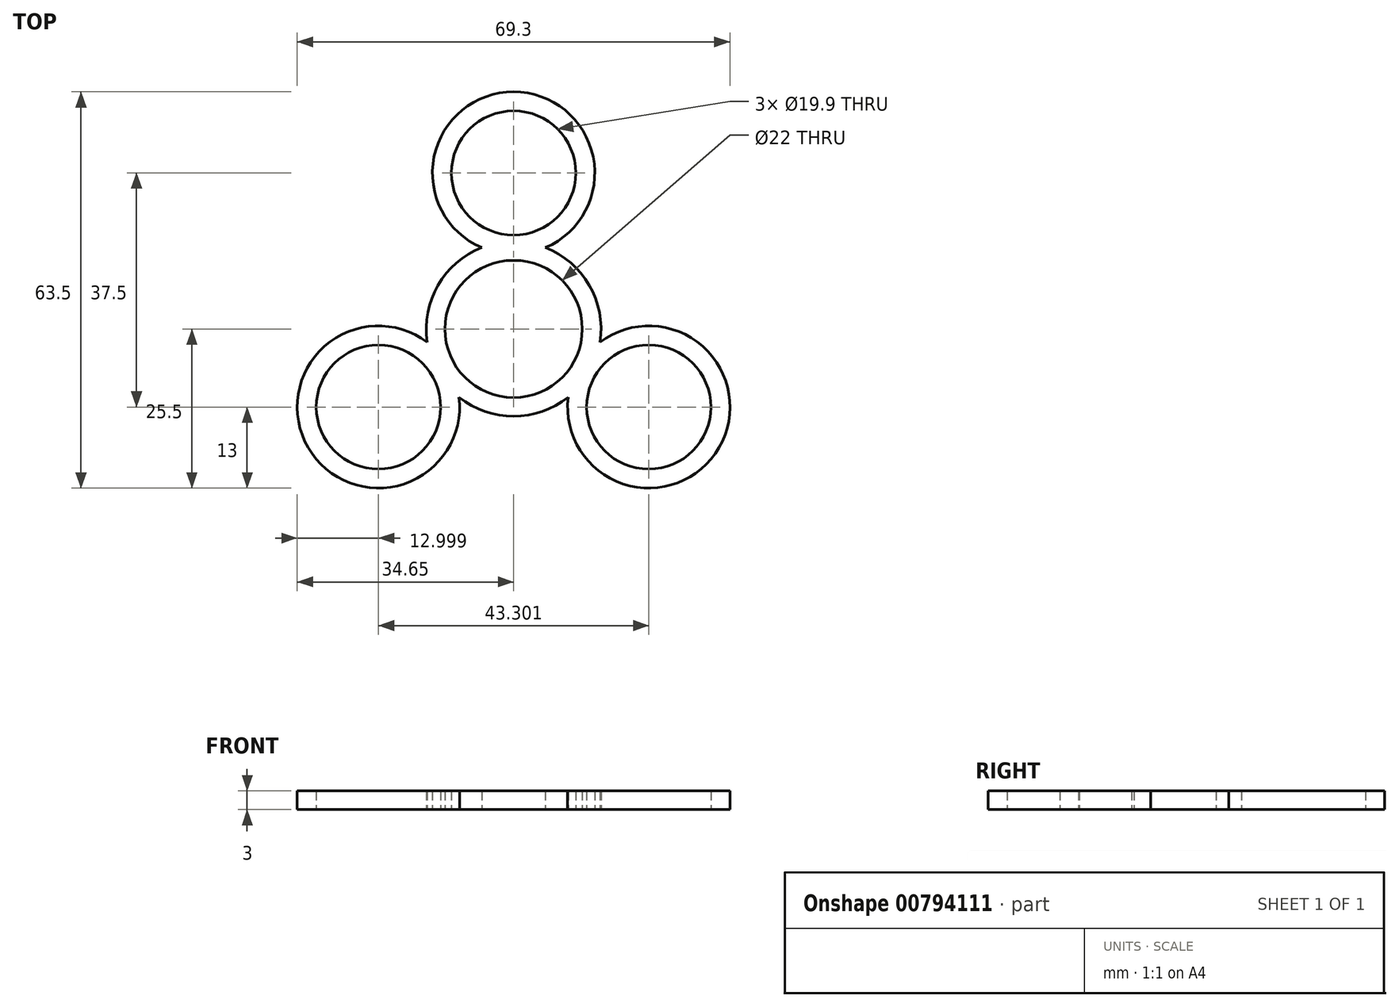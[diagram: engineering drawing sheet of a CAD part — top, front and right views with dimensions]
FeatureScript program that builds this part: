
annotation { "Feature Type Name" : "Feature", "Feature Type Description" : "" }
export const myFeature = defineFeature(function(context is Context, id is Id, definition is map)
    precondition{}
    {
        {
            var Q0;
            Q0=qCreatedBy(makeId("Top.planeOp"),FACE);
            var sketch = newSketch(context, id + "F0", { "sketchPlane" : qUnion([Q0])});
            skCircle(sketch, "E0", {"center": v(0, 0) * mm, "radius": 11 * mm});
            skArc(sketch, "E1", {"start": v(-5.1, 13.04) * mm, "mid": v(-12.12, 7) * mm, "end": v(-13.84, -2.1) * mm});
            skCircle(sketch, "E2", {"center": v(0, 25) * mm, "radius": 9.95 * mm});
            skArc(sketch, "E3", {"start": v(5.1, 13.04) * mm, "mid": v(0, 38) * mm, "end": v(-5.1, 13.04) * mm});
            skCircle(sketch, "E4.1.0", {"center": v(-21.65, -12.5) * mm, "radius": 9.95 * mm});
            skArc(sketch, "E4.1.1", {"start": v(-13.84, -2.1) * mm, "mid": v(-32.9, -19) * mm, "end": v(-8.75, -10.93) * mm});
            skCircle(sketch, "E4.2.0", {"center": v(21.65, -12.5) * mm, "radius": 9.95 * mm});
            skArc(sketch, "E4.2.1", {"start": v(8.75, -10.93) * mm, "mid": v(32.9, -19) * mm, "end": v(13.84, -2.1) * mm});
            skArc(sketch, "E5.trimOffspring", {"start": v(13.84, -2.1) * mm, "mid": v(12.12, 7) * mm, "end": v(5.1, 13.04) * mm});
            skArc(sketch, "E6.trimOffspring", {"start": v(-8.75, -10.93) * mm, "mid": v(0, -14) * mm, "end": v(8.75, -10.93) * mm});
            skSolve(sketch);
        }
        {
            var Q0;
            Q0 = qSketchRegion(id + "F0", true);
            extrude(context, id + "F1", {"entities" : qUnion([Q0]), "depth" : 3 * mm, "offsetDistance" : 25 * mm});
        }
    });
